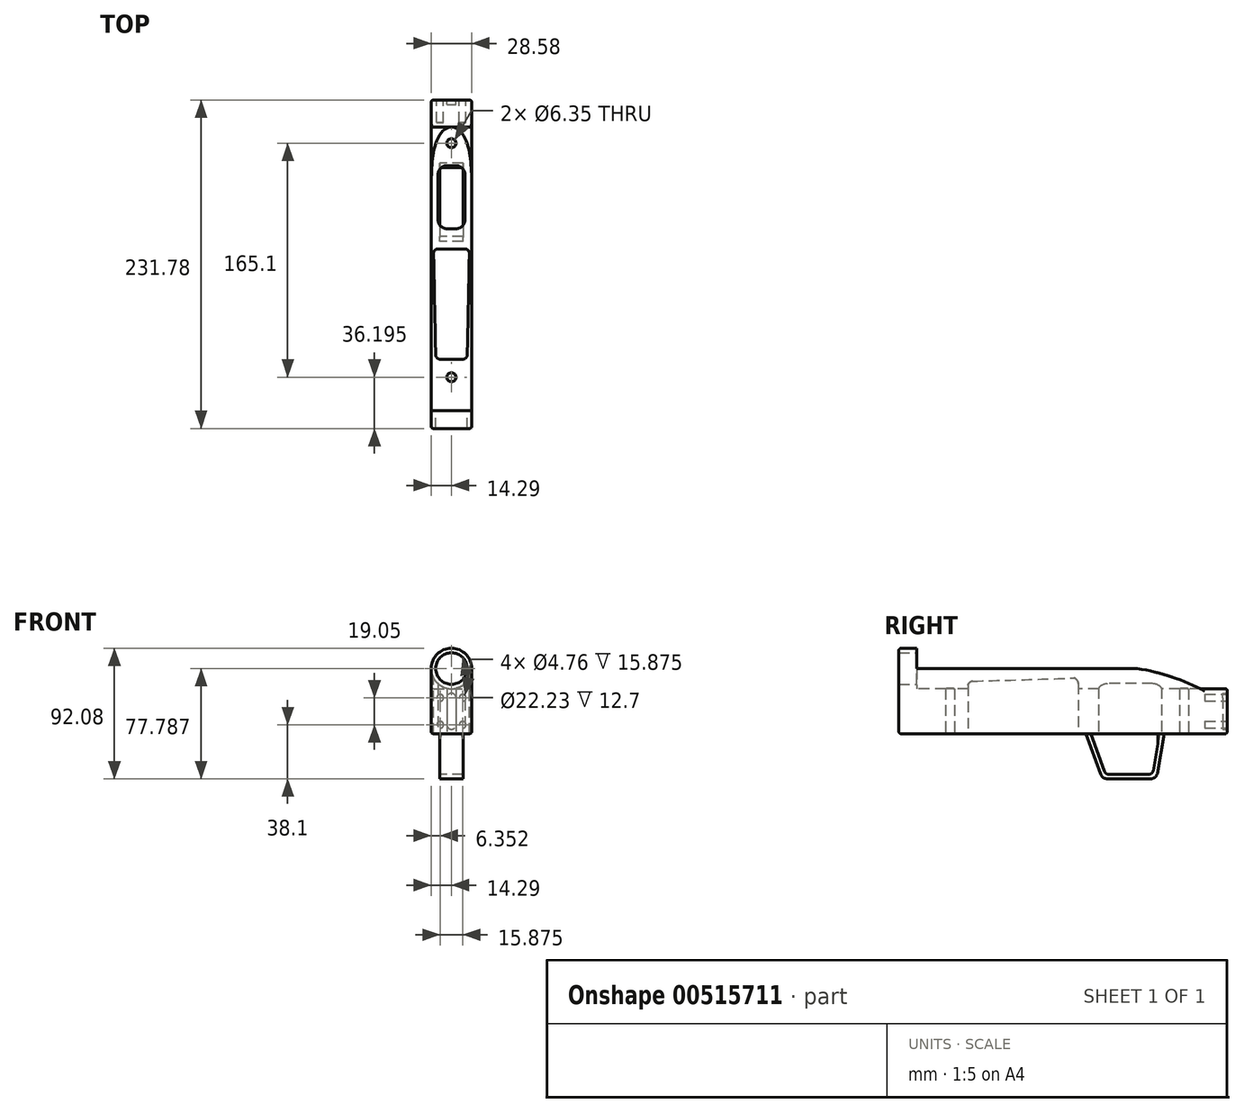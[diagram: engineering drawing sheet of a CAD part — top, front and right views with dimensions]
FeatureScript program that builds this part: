
annotation { "Feature Type Name" : "Feature", "Feature Type Description" : "" }
export const myFeature = defineFeature(function(context is Context, id is Id, definition is map)
    precondition{}
    {
        {
            var Q0;
            Q0=qCreatedBy(makeId("Front.planeOp"),FACE);
            var sketch = newSketch(context, id + "F0", { "sketchPlane" : qUnion([Q0])});
            skLineSegment(sketch, "E0", {"start": v(0, 67.11) * mm, "end": v(0, -56.79) * mm, "construction": true});
            skLineSegment(sketch, "E1", {"start": v(-61.95, 0) * mm, "end": v(62.78, 0) * mm, "construction": true});
            skLineSegment(sketch, "E2", {"start": v(-14.29, 46.04) * mm, "end": v(-14.29, 0) * mm});
            skLineSegment(sketch, "E3", {"start": v(-14.29, 0) * mm, "end": v(14.29, 0) * mm});
            skLineSegment(sketch, "E4", {"start": v(14.29, 0) * mm, "end": v(14.29, 46.04) * mm});
            skArc(sketch, "E5", {"start": v(14.29, 46.04) * mm, "mid": v(0, 60.33) * mm, "end": v(-14.29, 46.04) * mm});
            skCircle(sketch, "E6", {"center": v(0, 46.04) * mm, "radius": 11.11 * mm});
            skSolve(sketch);
        }
        {
            var Q0;
            Q0=makeQuery(id+"F0.imprint","IMPRINT",FACE,{"disambiguationData":[TD([[makeQuery(id+"F0.imprint","IMPRINT",EDGE,{"derivedFrom":sQuery(id+"F0.wireOp",EDGE,"E2")}),1.0]])]});
            extrude(context, id + "F1", {"entities" : qUnion([Q0]), "depth" : 12.7 * mm, "offsetDistance" : 25.4 * mm, "hasSecondDirection" : true, "secondDirectionOppositeDirection" : true, "secondDirectionDepth" : 200.02 * mm});
        }
        {
            var Q0;
            Q0=qCreatedBy(makeId("Front.planeOp"),FACE);
            var sketch = newSketch(context, id + "F2", { "sketchPlane" : qUnion([Q0])});
            skCircle(sketch, "E7", {"center": v(0, 46.04) * mm, "radius": 14.29 * mm});
            skArc(sketch, "E8.0", {"start": v(14.29, 46.04) * mm, "mid": v(0, 60.33) * mm, "end": v(-14.29, 46.04) * mm});
            skSolve(sketch);
        }
        {
            var Q0;
            Q0 = qSketchRegion(id + "F2", true);
            var Q1;
            Q1=makeQuery(id+"F1.opExtrude","CAP_FACE",FACE,{"disambiguationData":[OSD([sQuery(id+"F0.wireOp",EDGE,"E2"),sQuery(id+"F0.wireOp",EDGE,"E3"),sQuery(id+"F0.wireOp",EDGE,"E4"),sQuery(id+"F0.wireOp",EDGE,"E5"),sQuery(id+"F0.wireOp",EDGE,"E6")])],"isStart":true});
            extrude(context, id + "F3", {"entities" : qUnion([Q0]), "operationType" : NewBodyOperationType.REMOVE, "endBound" : BoundingType.UP_TO_SURFACE, "oppositeDirection" : true, "depth" : 25.4 * mm, "endBoundEntityFace" : qUnion([Q1]), "offsetDistance" : 25.4 * mm});
        }
        {
            var Q0;
            Q0=qCreatedBy(makeId("Right.planeOp"),FACE);
            var sketch = newSketch(context, id + "F4", { "sketchPlane" : qUnion([Q0])});
            skLineSegment(sketch, "E9.0", {"start": v(200.03, 31.75) * mm, "end": v(200.03, 46.04) * mm});
            skLineSegment(sketch, "E10.0", {"start": v(155.58, 46.04) * mm, "end": v(200.03, 46.04) * mm});
            skArc(sketch, "E11", {"start": v(200.03, 31.75) * mm, "mid": v(178.35, 40.6) * mm, "end": v(155.58, 46.04) * mm});
            skPoint(sketch, "E12.orphan", {"position": v(0, 46.04) * mm});
            skPoint(sketch, "E13.orphan", {"position": v(200.03, 0) * mm});
            skSolve(sketch);
        }
        {
            var Q0;
            Q0 = qSketchRegion(id + "F4", true);
            var Q1;
            Q1=makeQuery(id+"F1.opExtrude","SWEPT_FACE",FACE,{"disambiguationData":[OSD([sQuery(id+"F0.wireOp",EDGE,"E2")])]});
            var Q2;
            Q2=makeQuery(id+"F1.opExtrude","SWEPT_FACE",FACE,{"disambiguationData":[OSD([sQuery(id+"F0.wireOp",EDGE,"E4")])]});
            extrude(context, id + "F5", {"entities" : qUnion([Q0]), "operationType" : NewBodyOperationType.REMOVE, "endBound" : BoundingType.UP_TO_SURFACE, "oppositeDirection" : true, "depth" : 25.4 * mm, "endBoundEntityFace" : qUnion([Q1]), "offsetDistance" : 25.4 * mm, "hasSecondDirection" : true, "secondDirectionBound" : SecondDirectionBoundingType.UP_TO_SURFACE, "secondDirectionOppositeDirection" : false, "secondDirectionDepth" : 25.4 * mm, "secondDirectionBoundEntityFace" : qUnion([Q2])});
        }
        {
            var Q0;
            Q0=qCreatedBy(makeId("Top.planeOp"),FACE);
            var sketch = newSketch(context, id + "F6", { "sketchPlane" : qUnion([Q0])});
            skLineSegment(sketch, "E14", {"start": v(-44.68, 0) * mm, "end": v(40.66, 0) * mm, "construction": true});
            skLineSegment(sketch, "E15", {"start": v(0, -24.7) * mm, "end": v(0, 156.8) * mm, "construction": true});
            skCircle(sketch, "E16", {"center": v(0, 23.5) * mm, "radius": 3.18 * mm});
            skCircle(sketch, "E17", {"center": v(0, 188.6) * mm, "radius": 3.18 * mm});
            skLineSegment(sketch, "E18.0", {"start": v(-14.29, 200.03) * mm, "end": v(0, 200.03) * mm, "construction": true});
            skFitSpline(sketch, "E19.0.0", {"points": [v(-14.29, 107.95) * mm, v(-14.29, 110.1) * mm, v(-14.26, 114.39) * mm, v(-14.09, 120.74) * mm, v(-13.76, 125.96) * mm, v(-13.32, 130.09) * mm, v(-12.95, 132.65) * mm, v(-12.6, 134.68) * mm, v(-12.18, 136.71) * mm, v(-11.57, 139.2) * mm, v(-10.63, 142.11) * mm, v(-9.64, 144.45) * mm, v(-8.66, 146.26) * mm, v(-7.97, 147.35) * mm, v(-7.36, 148.18) * mm, v(-6.7, 148.98) * mm, v(-5.99, 149.74) * mm, v(-5.2, 150.42) * mm, v(-4.57, 150.9) * mm, v(-3.89, 151.33) * mm, v(-3.17, 151.7) * mm, v(-2.42, 152) * mm, v(-1.36, 152.3) * mm, v(-0.55, 152.4) * mm, v(0, 152.4) * mm], "construction": true});
            skLineSegment(sketch, "E19.0.1", {"start": v(0, 200.03) * mm, "end": v(-14.29, 200.03) * mm, "construction": true});
            skLineSegment(sketch, "E19.0.2", {"start": v(-14.29, 155.58) * mm, "end": v(-14.29, 200.03) * mm, "construction": true});
            skSolve(sketch);
        }
        {
            var Q0;
            Q0 = qSketchRegion(id + "F6", true);
            var Q1;
            Q1=makeQuery(id+"F3.boolean.opBoolean","COPY",FACE,{"derivedFrom":makeQuery(id+"F3.opExtrude","SWEPT_FACE",FACE,{"disambiguationData":[OSD([sQuery(id+"F2.wireOp",EDGE,"E7")])]})});
            extrude(context, id + "F7", {"entities" : qUnion([Q0]), "operationType" : NewBodyOperationType.REMOVE, "endBound" : BoundingType.UP_TO_SURFACE, "depth" : 25.4 * mm, "endBoundEntityFace" : qUnion([Q1]), "offsetDistance" : 25.4 * mm});
        }
        {
            var Q0;
            Q0=qCreatedBy(makeId("Right.planeOp"),FACE);
            var sketch = newSketch(context, id + "F8", { "sketchPlane" : qUnion([Q0])});
            skLineSegment(sketch, "E20", {"start": v(174.62, 0) * mm, "end": v(169.72, -27.81) * mm});
            skLineSegment(sketch, "E21", {"start": v(165.03, -31.75) * mm, "end": v(134.26, -31.75) * mm});
            skLineSegment(sketch, "E22", {"start": v(129.79, -28.62) * mm, "end": v(119.37, 0) * mm});
            skLineSegment(sketch, "E23.0.0", {"start": v(200.03, 0) * mm, "end": v(200.03, 31.75) * mm, "construction": true});
            skArc(sketch, "E23.0.1", {"start": v(200.03, 31.75) * mm, "mid": v(178.35, 40.6) * mm, "end": v(155.57, 46.04) * mm, "construction": true});
            skLineSegment(sketch, "E23.0.2", {"start": v(155.58, 46.04) * mm, "end": v(0, 46.04) * mm, "construction": true});
            skLineSegment(sketch, "E23.0.3", {"start": v(0, 46.04) * mm, "end": v(-12.7, 46.04) * mm, "construction": true});
            skLineSegment(sketch, "E23.0.4", {"start": v(-12.7, 46.04) * mm, "end": v(-12.7, 0) * mm, "construction": true});
            skLineSegment(sketch, "E23.0.5", {"start": v(-12.7, 0) * mm, "end": v(200.03, 0) * mm, "construction": true});
            skPoint(sketch, "E24.visualSharp", {"position": v(169.03, -31.75) * mm});
            skArc(sketch, "E24.filletArc", {"start": v(165.03, -31.75) * mm, "mid": v(168.1, -30.64) * mm, "end": v(169.72, -27.81) * mm});
            skPoint(sketch, "E25.visualSharp", {"position": v(130.93, -31.75) * mm});
            skArc(sketch, "E25.filletArc", {"start": v(129.79, -28.62) * mm, "mid": v(131.53, -30.89) * mm, "end": v(134.26, -31.75) * mm});
            skLineSegment(sketch, "E26.0", {"start": v(133.15, -28.57) * mm, "end": v(122.75, 0) * mm});
            skLineSegment(sketch, "E26.1", {"start": v(166.36, -28.57) * mm, "end": v(133.15, -28.57) * mm});
            skLineSegment(sketch, "E26.2", {"start": v(171.4, 0) * mm, "end": v(166.36, -28.57) * mm});
            skLineSegment(sketch, "E27", {"start": v(119.37, 0) * mm, "end": v(122.75, 0) * mm});
            skLineSegment(sketch, "E28", {"start": v(171.4, 0) * mm, "end": v(174.62, 0) * mm});
            skSolve(sketch);
        }
        {
            var Q0;
            Q0 = qSketchRegion(id + "F8", true);
            extrude(context, id + "F9", {"entities" : qUnion([Q0]), "operationType" : NewBodyOperationType.ADD, "depth" : 8.25 * mm, "offsetDistance" : 25.4 * mm, "hasSecondDirection" : true, "secondDirectionOppositeDirection" : true, "secondDirectionDepth" : 8.25 * mm});
        }
        {
            var Q0;
            Q0=makeQuery(id+"F1.opExtrude","CAP_FACE",FACE,{"disambiguationData":[OSD([sQuery(id+"F0.wireOp",EDGE,"E2"),sQuery(id+"F0.wireOp",EDGE,"E3"),sQuery(id+"F0.wireOp",EDGE,"E4"),sQuery(id+"F0.wireOp",EDGE,"E5"),sQuery(id+"F0.wireOp",EDGE,"E6")])],"isStart":true});
            var sketch = newSketch(context, id + "F10", { "sketchPlane" : qUnion([Q0])});
            skLineSegment(sketch, "E29.0.0", {"start": v(14.29, 0) * mm, "end": v(14.29, 31.75) * mm});
            skLineSegment(sketch, "E29.0.1", {"start": v(14.29, 31.75) * mm, "end": v(0, 31.75) * mm});
            skLineSegment(sketch, "E29.0.2", {"start": v(0, 31.75) * mm, "end": v(-14.29, 31.75) * mm});
            skLineSegment(sketch, "E29.0.3", {"start": v(-14.29, 31.75) * mm, "end": v(-14.29, 0) * mm});
            skLineSegment(sketch, "E29.0.4", {"start": v(-14.29, 0) * mm, "end": v(14.29, 0) * mm});
            skSolve(sketch);
        }
        {
            var Q0;
            Q0 = qSketchRegion(id + "F10", true);
            extrude(context, id + "F11", {"entities" : qUnion([Q0]), "operationType" : NewBodyOperationType.ADD, "depth" : 19.05 * mm, "offsetDistance" : 25.4 * mm});
        }
        {
            var Q0;
            Q0=makeQuery(id+"F11.opExtrude","CAP_FACE",FACE,{"disambiguationData":[OSD([sQuery(id+"F10.wireOp",EDGE,"E29.0.0"),sQuery(id+"F10.wireOp",EDGE,"E29.0.1"),sQuery(id+"F10.wireOp",EDGE,"E29.0.2"),sQuery(id+"F10.wireOp",EDGE,"E29.0.3"),sQuery(id+"F10.wireOp",EDGE,"E29.0.4")])],"isStart":false});
            var sketch = newSketch(context, id + "F12", { "sketchPlane" : qUnion([Q0])});
            skLineSegment(sketch, "E30", {"start": v(0, 31.75) * mm, "end": v(0, 0) * mm, "construction": true});
            skLineSegment(sketch, "E31", {"start": v(-14.29, 15.88) * mm, "end": v(14.29, 15.88) * mm, "construction": true});
            skArc(sketch, "E32", {"start": v(3.18, 25.4) * mm, "mid": v(0, 28.58) * mm, "end": v(-3.17, 25.4) * mm});
            skArc(sketch, "E33", {"start": v(-3.17, 6.35) * mm, "mid": v(0, 3.18) * mm, "end": v(3.18, 6.35) * mm});
            skLineSegment(sketch, "E34", {"start": v(-3.18, 25.4) * mm, "end": v(-3.17, 6.35) * mm});
            skLineSegment(sketch, "E35", {"start": v(3.17, 25.4) * mm, "end": v(3.18, 6.35) * mm});
            skSolve(sketch);
        }
        {
            var Q0;
            Q0 = qSketchRegion(id + "F12", true);
            extrude(context, id + "F13", {"entities" : qUnion([Q0]), "operationType" : NewBodyOperationType.REMOVE, "oppositeDirection" : true, "depth" : 3.17 * mm, "offsetDistance" : 25.4 * mm});
        }
        {
            var Q0;
            Q0=makeQuery(id+"F11.opExtrude","CAP_FACE",FACE,{"disambiguationData":[OSD([sQuery(id+"F10.wireOp",EDGE,"E29.0.0"),sQuery(id+"F10.wireOp",EDGE,"E29.0.1"),sQuery(id+"F10.wireOp",EDGE,"E29.0.2"),sQuery(id+"F10.wireOp",EDGE,"E29.0.3"),sQuery(id+"F10.wireOp",EDGE,"E29.0.4")])],"isStart":false});
            var sketch = newSketch(context, id + "F14", { "sketchPlane" : qUnion([Q0])});
            skLineSegment(sketch, "E36.0", {"start": v(-14.29, 0) * mm, "end": v(-14.29, 31.75) * mm, "construction": true});
            skLineSegment(sketch, "E37.0", {"start": v(14.29, 31.75) * mm, "end": v(-14.29, 31.75) * mm, "construction": true});
            skLineSegment(sketch, "E38.0", {"start": v(14.29, 31.75) * mm, "end": v(14.29, 0) * mm, "construction": true});
            skLineSegment(sketch, "E39.0", {"start": v(14.29, 0) * mm, "end": v(-14.29, 0) * mm, "construction": true});
            skLineSegment(sketch, "E40.0", {"start": v(-7.94, 6.35) * mm, "end": v(-7.94, 25.4) * mm, "construction": true});
            skLineSegment(sketch, "E40.1", {"start": v(7.94, 6.35) * mm, "end": v(-7.94, 6.35) * mm, "construction": true});
            skLineSegment(sketch, "E40.2", {"start": v(7.94, 25.4) * mm, "end": v(7.94, 6.35) * mm, "construction": true});
            skLineSegment(sketch, "E40.3", {"start": v(7.94, 25.4) * mm, "end": v(-7.94, 25.4) * mm, "construction": true});
            skCircle(sketch, "E41", {"center": v(-7.94, 25.4) * mm, "radius": 2.38 * mm});
            skCircle(sketch, "E42", {"center": v(7.94, 25.4) * mm, "radius": 2.38 * mm});
            skCircle(sketch, "E43", {"center": v(7.94, 6.35) * mm, "radius": 2.38 * mm});
            skCircle(sketch, "E44", {"center": v(-7.94, 6.35) * mm, "radius": 2.38 * mm});
            skSolve(sketch);
        }
        {
            var Q0;
            Q0 = qSketchRegion(id + "F14", true);
            extrude(context, id + "F15", {"entities" : qUnion([Q0]), "operationType" : NewBodyOperationType.REMOVE, "oppositeDirection" : true, "depth" : 15.88 * mm, "offsetDistance" : 25.4 * mm});
        }
        {
            var Q0;
            Q0=qCreatedBy(makeId("Top.planeOp"),FACE);
            var sketch = newSketch(context, id + "F16", { "sketchPlane" : qUnion([Q0])});
            skLineSegment(sketch, "E45.bottom", {"start": v(-9.52, 172.72) * mm, "end": v(9.52, 172.72) * mm});
            skLineSegment(sketch, "E45.top", {"start": v(-9.52, 128.27) * mm, "end": v(9.52, 128.27) * mm});
            skLineSegment(sketch, "E45.left", {"start": v(-9.53, 172.72) * mm, "end": v(-9.53, 128.27) * mm});
            skLineSegment(sketch, "E45.right", {"start": v(9.52, 172.72) * mm, "end": v(9.52, 128.27) * mm});
            skLineSegment(sketch, "E46", {"start": v(0, 154.08) * mm, "end": v(0, 24.38) * mm, "construction": true});
            skSolve(sketch);
        }
        {
            var Q0;
            Q0 = qSketchRegion(id + "F16", true);
            var Q1;
            Q1=makeQuery(id+"F3.boolean.opBoolean","COPY",FACE,{"derivedFrom":makeQuery(id+"F3.opExtrude","SWEPT_FACE",FACE,{"disambiguationData":[OSD([sQuery(id+"F2.wireOp",EDGE,"E7")])]})});
            var Q2;
            Q2=makeQuery(id+"F11.boolean.opBoolean","MERGE",FACE,{"derivedFrom":[makeQuery(id+"F1.opExtrude","SWEPT_FACE",FACE,{"disambiguationData":[OSD([sQuery(id+"F0.wireOp",EDGE,"E3")])]}),makeQuery(id+"F11.opExtrude","SWEPT_FACE",FACE,{"disambiguationData":[OSD([sQuery(id+"F10.wireOp",EDGE,"E29.0.4")])]})]});
            extrude(context, id + "F17", {"entities" : qUnion([Q0]), "operationType" : NewBodyOperationType.REMOVE, "endBound" : BoundingType.UP_TO_SURFACE, "depth" : 25.4 * mm, "endBoundEntityFace" : qUnion([Q1]), "offsetDistance" : 1.6 * mm});
        }
        {
            var Q0;
            Q0=qCreatedBy(makeId("Top.planeOp"),FACE);
            var sketch = newSketch(context, id + "F18", { "sketchPlane" : qUnion([Q0])});
            skLineSegment(sketch, "E47", {"start": v(0, 0) * mm, "end": v(0, 178.6) * mm, "construction": true});
            skLineSegment(sketch, "E48", {"start": v(-12.7, 113.98) * mm, "end": v(-11.11, 36.2) * mm});
            skLineSegment(sketch, "E49", {"start": v(-11.11, 36.2) * mm, "end": v(11.11, 36.2) * mm});
            skLineSegment(sketch, "E50", {"start": v(11.11, 36.2) * mm, "end": v(12.7, 113.98) * mm});
            skLineSegment(sketch, "E51", {"start": v(12.7, 113.98) * mm, "end": v(-12.7, 113.98) * mm});
            skSolve(sketch);
        }
        {
            var Q0;
            Q0 = qSketchRegion(id + "F18", true);
            var Q1;
            Q1=makeQuery(id+"F3.boolean.opBoolean","COPY",FACE,{"derivedFrom":makeQuery(id+"F3.opExtrude","SWEPT_FACE",FACE,{"disambiguationData":[OSD([sQuery(id+"F2.wireOp",EDGE,"E7")])]})});
            extrude(context, id + "F19", {"entities" : qUnion([Q0]), "operationType" : NewBodyOperationType.REMOVE, "endBound" : BoundingType.UP_TO_SURFACE, "depth" : 25.4 * mm, "endBoundEntityFace" : qUnion([Q1]), "offsetDistance" : 25.4 * mm});
        }
        {
            var Q0;
            Q0=makeQuery(id+"F17.boolean.opBoolean","COPY",EDGE,{"derivedFrom":makeQuery(id+"F17.opExtrude","SWEPT_EDGE",EDGE,{"disambiguationData":[OSD([sQuery(id+"F16.wireOp",EDGE,"E45.top"),sQuery(id+"F16.wireOp",EDGE,"E45.right")])]})});
            var Q1;
            Q1=makeQuery(id+"F17.boolean.opBoolean","COPY",EDGE,{"derivedFrom":makeQuery(id+"F17.opExtrude","SWEPT_EDGE",EDGE,{"disambiguationData":[OSD([sQuery(id+"F16.wireOp",EDGE,"E45.top"),sQuery(id+"F16.wireOp",EDGE,"E45.left")])]})});
            var Q2;
            Q2=makeQuery(id+"F17.boolean.opBoolean","COPY",EDGE,{"derivedFrom":makeQuery(id+"F17.opExtrude","SWEPT_EDGE",EDGE,{"disambiguationData":[OSD([sQuery(id+"F16.wireOp",EDGE,"E45.bottom"),sQuery(id+"F16.wireOp",EDGE,"E45.left")])]})});
            var Q3;
            Q3=makeQuery(id+"F17.boolean.opBoolean","COPY",EDGE,{"derivedFrom":makeQuery(id+"F17.opExtrude","SWEPT_EDGE",EDGE,{"disambiguationData":[OSD([sQuery(id+"F16.wireOp",EDGE,"E45.bottom"),sQuery(id+"F16.wireOp",EDGE,"E45.right")])]})});
            fillet(context, id + "F20", {"entities" : qUnion([Q0, Q1, Q2, Q3]), "radius" : 6.35 * mm, "tangentPropagation" : true, "allowEdgeOverflow" : false});
        }
        {
            var Q0;
            Q0=makeQuery(id+"F19.boolean.opBoolean","COPY",EDGE,{"derivedFrom":makeQuery(id+"F19.opExtrude","SWEPT_EDGE",EDGE,{"disambiguationData":[OSD([sQuery(id+"F18.wireOp",EDGE,"E50"),sQuery(id+"F18.wireOp",EDGE,"E51")])]})});
            var Q1;
            Q1=makeQuery(id+"F19.boolean.opBoolean","COPY",EDGE,{"derivedFrom":makeQuery(id+"F19.opExtrude","SWEPT_EDGE",EDGE,{"disambiguationData":[OSD([sQuery(id+"F18.wireOp",EDGE,"E48"),sQuery(id+"F18.wireOp",EDGE,"E51")])]})});
            var Q2;
            Q2=makeQuery(id+"F19.boolean.opBoolean","COPY",EDGE,{"derivedFrom":makeQuery(id+"F19.opExtrude","SWEPT_EDGE",EDGE,{"disambiguationData":[OSD([sQuery(id+"F18.wireOp",EDGE,"E49"),sQuery(id+"F18.wireOp",EDGE,"E50")])]})});
            var Q3;
            Q3=makeQuery(id+"F19.boolean.opBoolean","COPY",EDGE,{"derivedFrom":makeQuery(id+"F19.opExtrude","SWEPT_EDGE",EDGE,{"disambiguationData":[OSD([sQuery(id+"F18.wireOp",EDGE,"E48"),sQuery(id+"F18.wireOp",EDGE,"E49")])]})});
            fillet(context, id + "F21", {"entities" : qUnion([Q0, Q1, Q2, Q3]), "radius" : 3.17 * mm, "tangentPropagation" : true, "allowEdgeOverflow" : false});
        }
        {
            var Q0;
            Q0=makeQuery(id+"F9.opExtrude","SWEPT_EDGE",EDGE,{"disambiguationData":[OSD([sQuery(id+"F8.wireOp",EDGE,"E26.0"),sQuery(id+"F8.wireOp",EDGE,"E27")])]});
            var Q1;
            Q1=makeQuery(id+"F9.opExtrude","SWEPT_EDGE",EDGE,{"disambiguationData":[OSD([sQuery(id+"F8.wireOp",EDGE,"E20"),sQuery(id+"F8.wireOp",EDGE,"E28")])]});
            var Q2;
            Q2=makeQuery(id+"F9.opExtrude","SWEPT_EDGE",EDGE,{"disambiguationData":[OSD([sQuery(id+"F8.wireOp",EDGE,"E26.2"),sQuery(id+"F8.wireOp",EDGE,"E28")])]});
            var Q3;
            Q3=makeQuery(id+"F9.opExtrude","SWEPT_EDGE",EDGE,{"disambiguationData":[OSD([sQuery(id+"F8.wireOp",EDGE,"E26.1"),sQuery(id+"F8.wireOp",EDGE,"E26.2")])]});
            var Q4;
            Q4=makeQuery(id+"F9.opExtrude","SWEPT_EDGE",EDGE,{"disambiguationData":[OSD([sQuery(id+"F8.wireOp",EDGE,"E26.0"),sQuery(id+"F8.wireOp",EDGE,"E26.1")])]});
            fillet(context, id + "F22", {"entities" : qUnion([Q0, Q1, Q2, Q3, Q4]), "radius" : 3.17 * mm, "tangentPropagation" : true, "allowEdgeOverflow" : false});
        }
        {
            var Q0;
            Q0=makeQuery(id+"F5.boolean.opBoolean","COPY",EDGE,{"derivedFrom":makeQuery(id+"F5.opExtrude","CAP_EDGE",EDGE,{"disambiguationData":[OSD([sQuery(id+"F4.wireOp",EDGE,"E11")])],"isStart":false})});
            var Q1;
            Q1=makeQuery(id+"F11.opExtrude","SWEPT_EDGE",EDGE,{"disambiguationData":[OSD([sQuery(id+"F10.wireOp",EDGE,"E29.0.0"),sQuery(id+"F10.wireOp",EDGE,"E29.0.1")])]});
            var Q2;
            Q2=makeQuery(id+"F5.boolean.opBoolean","COPY",EDGE,{"derivedFrom":makeQuery(id+"F5.opExtrude","CAP_EDGE",EDGE,{"disambiguationData":[OSD([sQuery(id+"F4.wireOp",EDGE,"E11")])],"isStart":true})});
            var Q3;
            Q3=makeQuery(id+"F11.opExtrude","SWEPT_EDGE",EDGE,{"disambiguationData":[OSD([sQuery(id+"F10.wireOp",EDGE,"E29.0.2"),sQuery(id+"F10.wireOp",EDGE,"E29.0.3")])]});
            var Q4;
            Q4=makeQuery(id+"F11.boolean.opBoolean","MERGE",EDGE,{"derivedFrom":[makeQuery(id+"F1.opExtrude","SWEPT_EDGE",EDGE,{"disambiguationData":[OSD([sQuery(id+"F0.wireOp",EDGE,"E2"),sQuery(id+"F0.wireOp",EDGE,"E3")])]}),makeQuery(id+"F11.opExtrude","SWEPT_EDGE",EDGE,{"disambiguationData":[OSD([sQuery(id+"F10.wireOp",EDGE,"E29.0.0"),sQuery(id+"F10.wireOp",EDGE,"E29.0.4")])]})]});
            var Q5;
            Q5=makeQuery(id+"F11.boolean.opBoolean","MERGE",EDGE,{"derivedFrom":[makeQuery(id+"F1.opExtrude","SWEPT_EDGE",EDGE,{"disambiguationData":[OSD([sQuery(id+"F0.wireOp",EDGE,"E3"),sQuery(id+"F0.wireOp",EDGE,"E4")])]}),makeQuery(id+"F11.opExtrude","SWEPT_EDGE",EDGE,{"disambiguationData":[OSD([sQuery(id+"F10.wireOp",EDGE,"E29.0.3"),sQuery(id+"F10.wireOp",EDGE,"E29.0.4")])]})]});
            var Q6;
            Q6=makeQuery(id+"F11.opExtrude","CAP_EDGE",EDGE,{"disambiguationData":[OSD([sQuery(id+"F10.wireOp",EDGE,"E29.0.4")])],"isStart":false});
            var Q7;
            Q7=makeQuery(id+"F11.opExtrude","CAP_EDGE",EDGE,{"disambiguationData":[OSD([sQuery(id+"F10.wireOp",EDGE,"E29.0.3")])],"isStart":false});
            var Q8;
            Q8=makeQuery(id+"F11.opExtrude","CAP_EDGE",EDGE,{"disambiguationData":[OSD([sQuery(id+"F10.wireOp",EDGE,"E29.0.0")])],"isStart":false});
            var Q9;
            Q9=makeQuery(id+"F11.opExtrude","CAP_EDGE",EDGE,{"disambiguationData":[OSD([sQuery(id+"F10.wireOp",EDGE,"E29.0.1"),sQuery(id+"F10.wireOp",EDGE,"E29.0.2")])],"isStart":false});
            var Q10;
            Q10=makeQuery(id+"F1.opExtrude","CAP_EDGE",EDGE,{"disambiguationData":[OSD([sQuery(id+"F0.wireOp",EDGE,"E3")])],"isStart":false});
            var Q11;
            Q11=makeQuery(id+"F1.opExtrude","CAP_EDGE",EDGE,{"disambiguationData":[OSD([sQuery(id+"F0.wireOp",EDGE,"E4")])],"isStart":false});
            fillet(context, id + "F23", {"entities" : qUnion([Q0, Q1, Q2, Q3, Q4, Q5, Q6, Q7, Q8, Q9, Q10, Q11]), "radius" : 1.59 * mm, "tangentPropagation" : true, "allowEdgeOverflow" : false});
        }
    });
